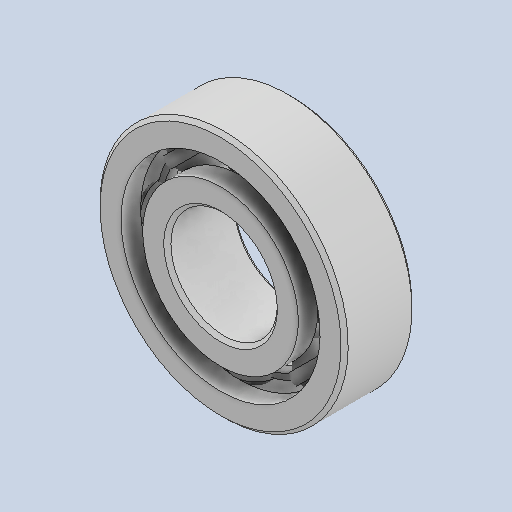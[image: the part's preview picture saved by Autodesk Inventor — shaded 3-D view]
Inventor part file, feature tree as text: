
AUTODESK INVENTOR PART (.ipt)
format: ipt  version: 2023 (Build 270158030, 158C)  size: 717,312 bytes
history: native  units: in
note: dims shown in document units (in); Inventor stores cm internally (conversion verified against a paired STEP export)
features: other x15, revolve x4
ambient origin geometry x8: Origin, YZ Plane, XZ Plane, XY Plane, X Axis, Y Axis, Z Axis, Center Point
bodies: Solid1 (feature_tree), Solid2 (feature_tree), Solid3 (feature_tree), Solid4 (feature_tree), Solid5 (feature_tree), Solid6 (feature_tree), Solid7 (feature_tree), Solid8 (feature_tree), Solid9 (feature_tree), Solid10 (feature_tree), Solid11 (feature_tree), Solid12 (feature_tree), Solid13 (feature_tree), Solid14 (feature_tree), Solid15 (feature_tree), Solid16 (feature_tree), Solid17 (feature_tree), Solid18 (feature_tree), Solid19 (feature_tree)
feature tree (19):
  revolve  "Revolve3"  [1 undecoded]
  revolve  "Revolve4"  [1 undecoded]
  revolve  "Revolve6"  [1 undecoded]
  other  "CirPattern1[1]"
  other  "CirPattern1[2]"
  other  "CirPattern1[3]"
  other  "CirPattern1[4]"
  other  "CirPattern1[5]"
  other  "CirPattern1[6]"
  other  "CirPattern1[7]"
  revolve  "Revolve7"  [1 undecoded]
  other  "CirPattern1[8]"
  other  "CirPattern1[9]"
  other  "CirPattern1[10]"
  other  "CirPattern1[11]"
  other  "CirPattern1[12]"
  other  "CirPattern1[13]"
  other  "CirPattern1[14]"
  other  "Boss-Extrude1"
note: 4 required parameter values undecoded (feature->parameter linkage not recoverable at this tier; creation-order binding heuristic only, values carry confidence <= 0.55)
